# Revit family: 3f_filippi_-_beta_235_76_vs_ampio_3f_filippi_-_52821_-_beta_235_led_761x60_dali_ampio_vs_l1565
name_source: partatom
category: Lighting Fixtures
units: mm (PartAtom-declared; Revit-internal decimal feet)

## family parameters
Cut with Voids When Loaded = No
Host = Face
Light Source = No
Part Type = Normal
Room Calculation Point = No
Round Connector Dimension = Use Diameter
Shared = No

## types (1)
- 3F Filippi - Beta 235 76 VS Ampio (1 x LED, 9355 lm, 65 W, 4000 K)
    Apparent Load = 65 VA
    Approval mark = CE
    CIE Flux Codes = 65 90 98 100 100
    Color Rendering = 80
    Color Temperature = 4000 K
    Control Gear = Electronic transformer
    Default Elevation = 1800 mm
    Description = ILLUMINOTECHNICAL
Luminous efficiency 100% (DLOR 100%, ULOR 0%).
Initial luminous flux of the luminaire 9355 lm.
Wide symmetric distribution.
Installation Interdistance Transv.D = 1.26 x hu - Long.D = 1.32 x hu.
Tabular UGR (CIE 117 - 4H-8H; S=0.25H; 70/50/20): RUG 20.1 - 21.1.
Beam angle: 87° - 91°.
Luminous efficacy 144 lm/W.
Lifetime (L93/B10): 30000 h. (tq+25°C)
Lifetime (L90/B10): 50000 h. (tq+25°C)
Lifetime (L85/B10): 80000 h. (tq+25°C)
Lifetime (L80/B10): 100000 h. (tq+25°C)
Lifetime (L85/B10): 50000 h. (tq+45°C)
Sudden decreased luminous flux after 50000 hours: 0% (C0).
Photobiological safety in compliance with IEC/TR 62778: RG0 risk exempt, (IEC 62471).
In compliance with IEC/EN 62722-2-1 - IEC/EN 62717 standards.

SOURCE
Linear LED module 60W/840.
Energy efficiency class (UE 2019/2020 - UE 2019/2015): C.
CIE 13.3 Colour rendering index: CRI >80 (R9 <50%).
IES TM-30 Fidelity Index: Rf = 84 Rg = 95.
CCT nominal colour temperature 4000 K.
Colour initial tolerance (MacAdam): SDCM 3.

MECHANICAL
Single-piece housing in pressed steel, powder-coated in white epoxy-polyester.
VS moulded anti-glare glass, non-combustible, single-piece perimeter frame in galvanised steel.
Ecologic anti-aging injected sealing gasket.
Oversized gear-tray reflector unit in highly reflective white painted hot-galvanised steel.
Methacrylate (PMMA) lenses with external flat surface.
Galvanised steel snap-lock clips for diffuser mounting (safety n° 4 per fixture).
Luminaire with limited surface temperature. - D - (EN 60598-2-24)
Dimensions: 1565x235 mm, height 105 mm. Weight 10.82 kg.
IP66 protection degree.
Mechanical strength to impacts IK09 (10 joule).
Glow-wire test resistance 960°C.

ELECTRICAL
Halogen Free DALI-2, PUSH-DIM, electronic wiring 230V-50/60Hz, power factor 0.95 at full load, THD <25%, constant output current, class I, 1 driver, 1 DALI addresse.
Power of the luminaire 65 W.
ENEC - CE.
Flicker: <4%.
Luminaire compliant with EN 60598-2-22 for power supply from a centralised emergency system CPSS (Central Power Supply System), not incorporated in the luminaire - high risk areas excluded. The default power and flux are 100% in AC and 15% in DC.
Ambient temperature from -20°C to +45°C.
Temperature class T6 max 85°C.
Quick connection via M25 5P connector with 9-13 mm tightening range.
Relative humidity UR: <85%.

INSTALLATION
Ceiling / Suspended / Wall.
All accessories dedicated to this product are available on the Catalog and on our website www.3F-Filippi.com.

APPLICATIONS
Dry, dusty indoor environments, subject to occasional water splashes.
Industrial environments, warehouses, environments where security locks are required on all clips, e.g. prisons (on request).
Environments in which it is necessary a total protection against falling fragments (eg environments with foodstuffs or machines with moving parts or with extreme temperature changes), use luminaires with laminated glass.
Tempered glass is not immune to falling fragments from harmless and caused by shocks or exceptionally derived from the tempering process.

LIGHT MANAGEMENT
Recommended minimum setting: 10%.
The device, equipped with DALI-2 driver, can be controlled manually with 3F Easy Dim technology or automatically/manually with 3F Smart Dimming technology and/or centralised DALI systems.
DALI-2 certification guarantees interoperability with other devices with the same certification.
In electrical systems without a regulation system (manual or automatic) and DALI bus, a suitable jumper must be made on the DA-DA terminals of the appliance.

WARNING
Fixture not suitable for cold stores with an ambient temperature <0°C and/or relative humidity >85%.
Luminaire designed for disposal/recycling at end-of-life.
Replaceable (LED only) light source by a professional. Replaceable control gear by a professional.
    Height = 105 mm
    Lamp = 1 x LED
    Lamp Light Flux = 9355 lm
    Lamp Power = 65 W
    Lamp count = 1
    Length = 1565 mm
    Lifetime = 50000 h
    Luminous efficacy = 144 lm/W
    Manufacturer = 3F Filippi
    ModVariant = No
    Model = 3F Filippi - 52821 - Beta 235 LED 761x60 DALI AMPIO VS L1565
    Mounting Place = Ceiling
    Mounting Type = Pendant
    Number of Poles = 1
    OnlyDefault = Yes
    Power Factor = 1
    Product Name = 3F Filippi - Beta 235 76 VS Ampio
    Product group = pendant luminaire
    ProductGroupID = 9
    Protection Class = Protection class I
    Protection Degree = IP 66
    RLX_Detail_Level = 1
    RLX_Emergency_Light_Flux = 0 lm
    RLX_Emergency_Type = 0
    RLX_Emergency_Type_DB = No
    RlxData = <blob elided: 82985 chars, md5=7994c3e6>
    Socket = socket
    Standby Power = 0 W
    System Light Flux = 9355 lm
    System Power = 65 W
    Type Comments = Product without accessories
    Type Image = 3ffilippi_52821.jpg
    URL = http://relux.com
    VarID = ---
    Voltage = 0 V
    Weight = 0.00 kg
    Width = 235 mm

## geometry (parser evidence)
native form markers: Sweep x12
no freeform markers — native parametric forms only
